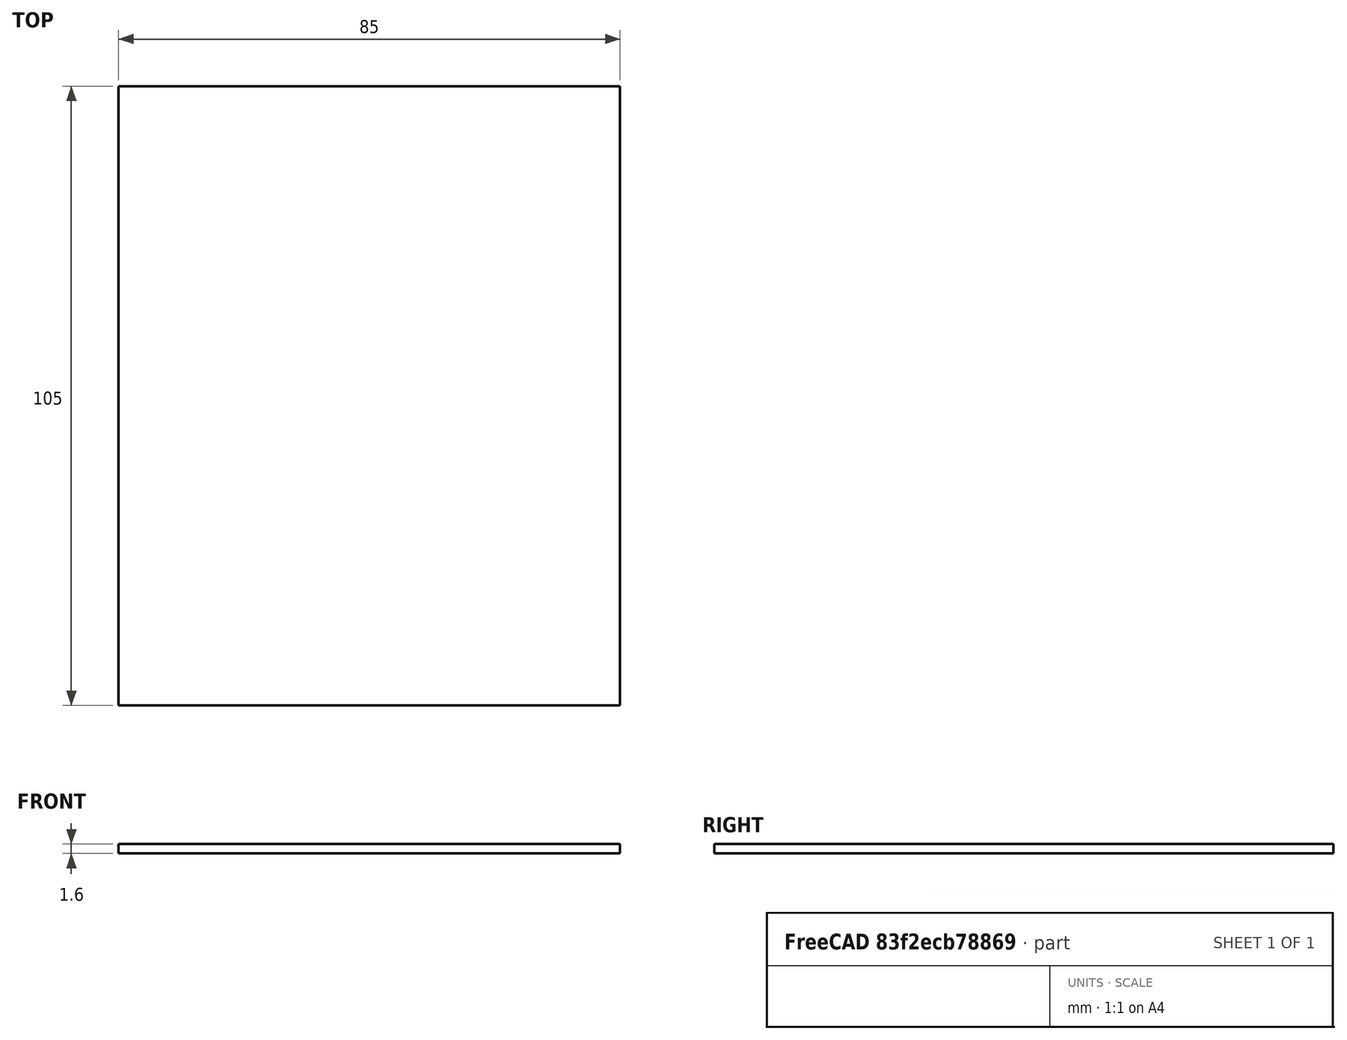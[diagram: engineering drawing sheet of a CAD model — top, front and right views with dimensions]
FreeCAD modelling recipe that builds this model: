
FCSTD DOCUMENT  (FreeCAD 0.21R33771 (Git))
Label: FDC
License: All rights reserved
LicenseURL: https://en.wikipedia.org/wiki/All_rights_reserved
objects: Sketcher::SketchObject×1, PartDesign::Pad×1, PartDesign::Body×1
note: 4 computed .brp shape members not serialized (recipe doc carries the construction recipe); baked Part::Feature solids carry a one-line shape summary decoded from their .brp

FEATURE [Sketcher::SketchObject] Sketch
  FullyConstrained = true
  MapMode = 5
  sketch-geometry (5):
    g0: LineSegment StartX=-42.5 StartY=52.5 StartZ=0 EndX=-42.5 EndY=-52.5 EndZ=0
    g1: LineSegment StartX=-42.5 StartY=-52.5 StartZ=0 EndX=42.5 EndY=-52.5 EndZ=0
    g2: LineSegment StartX=42.5 StartY=-52.5 StartZ=0 EndX=42.5 EndY=52.5 EndZ=0
    g3: LineSegment StartX=42.5 StartY=52.5 StartZ=0 EndX=-42.5 EndY=52.5 EndZ=0
    g4: GeomPoint X=0 Y=0 Z=0
  constraints (12):
    c: Coincident(g0,g1)
    c: Coincident(g1,g2)
    c: Coincident(g2,g3)
    c: Coincident(g3,g0)
    c: Vertical(g0)
    c: Vertical(g2)
    c: Horizontal(g1)
    c: Horizontal(g3)
    c: Symmetric(g2,g0,g4)
    c: Coincident(g4,g-1)
    c: DistanceX(g3,g3) = 85
    c: DistanceY(g0,g0) = 105
FEATURE [PartDesign::Pad] Pad
  Direction = (0,0,1)
  Length = 1.6
  Length2 = 10
  Placement = pos=(0,-192,0) rot=(0,0,1;0rad)
  Profile = -> Sketch
  ReferenceAxis = -> Sketch [N_Axis]
  Refine = true
  Type = 0
FEATURE [PartDesign::Body] Body
  Group = -> [Sketch,Pad]
  Origin = -> Origin
  Tip = -> Pad
